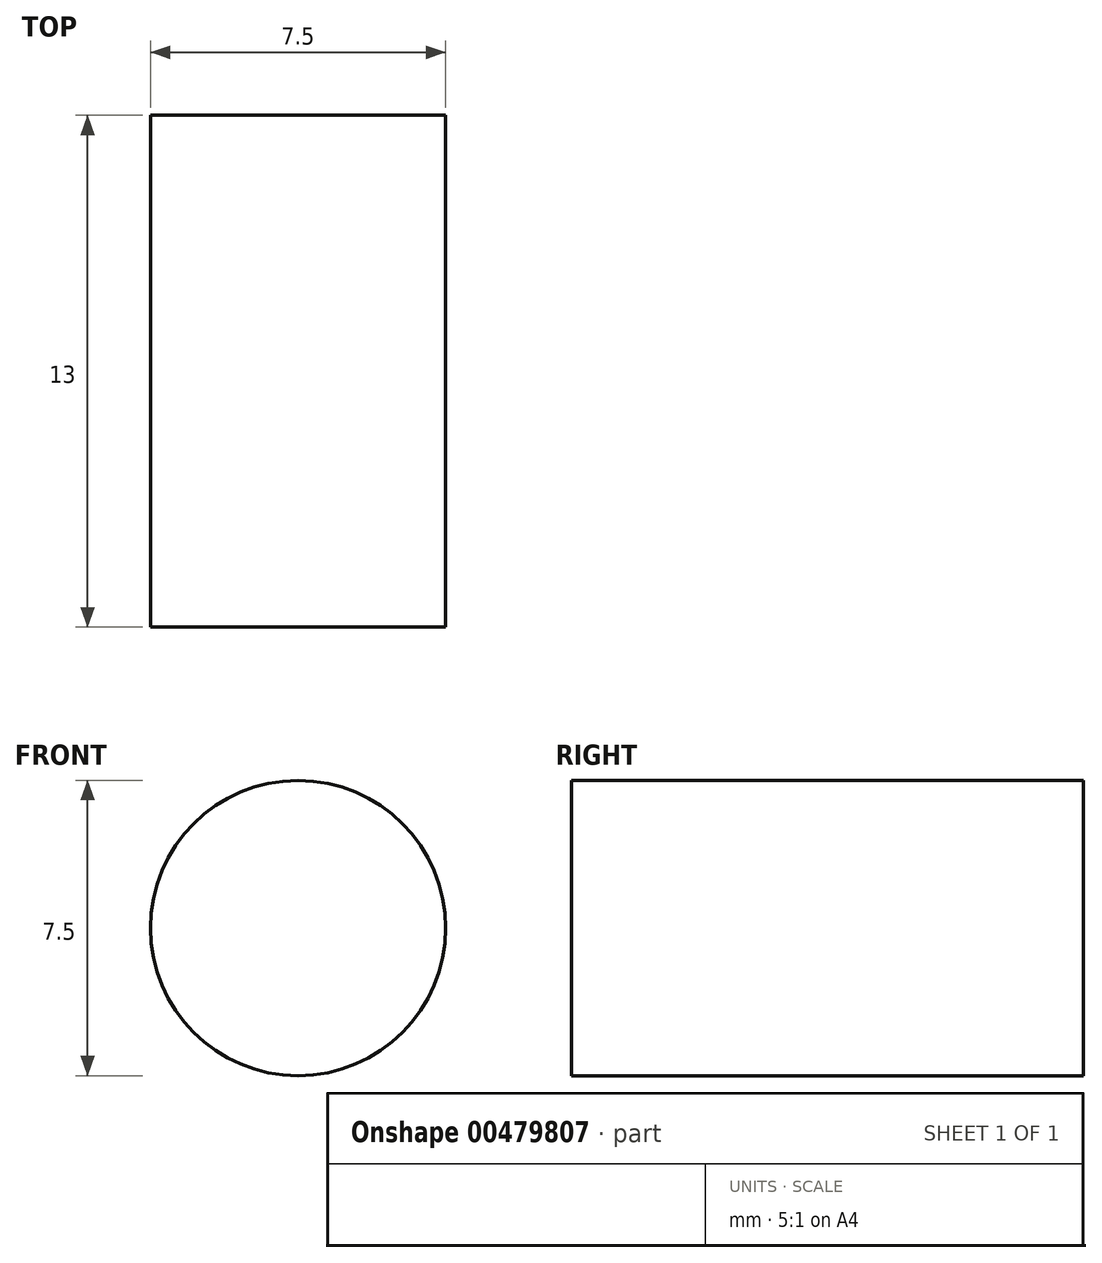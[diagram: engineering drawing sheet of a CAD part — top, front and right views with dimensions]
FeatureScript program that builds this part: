
annotation { "Feature Type Name" : "Feature", "Feature Type Description" : "" }
export const myFeature = defineFeature(function(context is Context, id is Id, definition is map)
    precondition{}
    {
        {
            var Q0;
            Q0=qCreatedBy(makeId("Front.planeOp"),FACE);
            var sketch = newSketch(context, id + "F0", { "sketchPlane" : qUnion([Q0])});
            skCircle(sketch, "E0", {"center": v(0, 0) * mm, "radius": 3.75 * mm});
            skSolve(sketch);
        }
        {
            var Q0;
            Q0=makeQuery(id+"F0.imprint","IMPRINT",FACE,{"disambiguationData":[TD([[makeQuery(id+"F0.imprint","IMPRINT",EDGE,{"derivedFrom":sQuery(id+"F0.wireOp",EDGE,"E0")}),1.0]])]});
            var Q1;
            Q1=sQuery(id+"F0.wireOp",EDGE,"E0");
            extrude(context, id + "F1", {"entities" : qUnion([Q0]), "surfaceEntities" : qUnion([Q1]), "depth" : 13 * mm});
        }
    });
